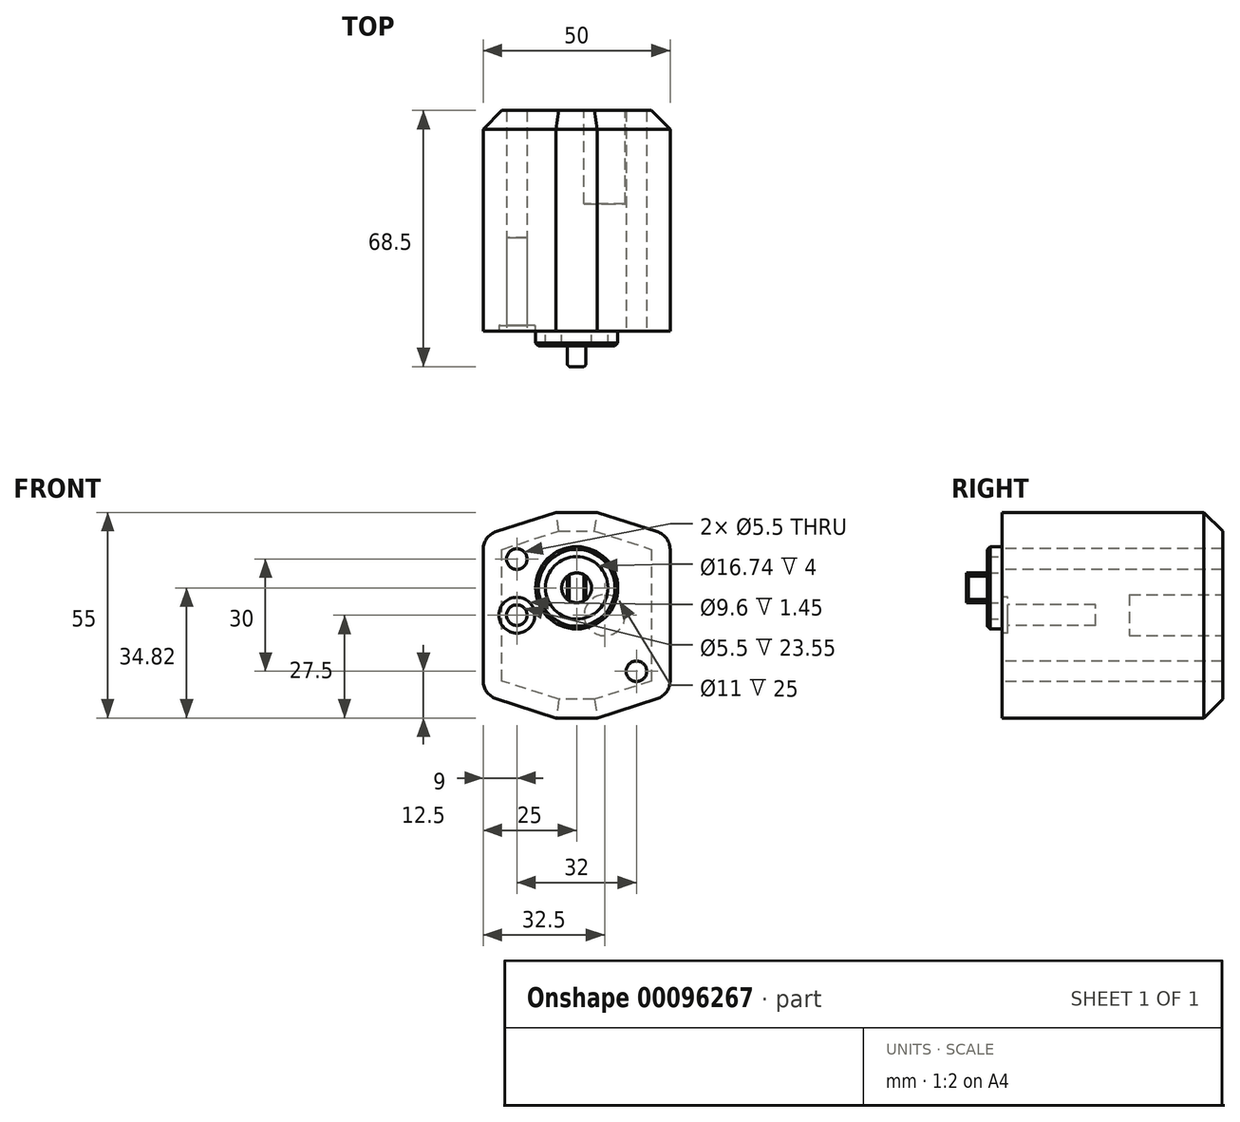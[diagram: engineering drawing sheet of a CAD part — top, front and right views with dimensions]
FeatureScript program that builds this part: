
annotation { "Feature Type Name" : "Feature", "Feature Type Description" : "" }
export const myFeature = defineFeature(function(context is Context, id is Id, definition is map)
    precondition{}
    {
        {
            var Q0;
            Q0=qCreatedBy(makeId("Front.planeOp"),FACE);
            var sketch = newSketch(context, id + "F0", { "sketchPlane" : qUnion([Q0])});
            skLineSegment(sketch, "E0", {"start": v(-25, -27.5) * mm, "end": v(25, -27.5) * mm});
            skLineSegment(sketch, "E1", {"start": v(25, -27.5) * mm, "end": v(25, 27.5) * mm});
            skLineSegment(sketch, "E2", {"start": v(25, 27.5) * mm, "end": v(-25, 27.5) * mm});
            skLineSegment(sketch, "E3", {"start": v(-25, 27.5) * mm, "end": v(-25, -27.5) * mm});
            skCircle(sketch, "E4", {"center": v(-16, 15) * mm, "radius": 2.75 * mm});
            skCircle(sketch, "E5", {"center": v(16, -15) * mm, "radius": 2.75 * mm});
            skCircle(sketch, "E6", {"center": v(-16, 0) * mm, "radius": 2.75 * mm});
            skCircle(sketch, "E7", {"center": v(0, 7.32) * mm, "radius": 4 * mm});
            skCircle(sketch, "E8", {"center": v(0, 7.32) * mm, "radius": 11 * mm});
            skLineSegment(sketch, "E9", {"start": v(-2.5, 10.44) * mm, "end": v(-2.5, 4.2) * mm});
            skLineSegment(sketch, "E10", {"start": v(2.5, 10.44) * mm, "end": v(2.5, 4.2) * mm});
            skCircle(sketch, "E11", {"center": v(0, 7.32) * mm, "radius": 8.37 * mm});
            skLineSegment(sketch, "E12", {"start": v(5.53, 27.5) * mm, "end": v(25, 21.23) * mm});
            skLineSegment(sketch, "E13.MirrorCS", {"start": v(5.53, -27.5) * mm, "end": v(25, -21.23) * mm});
            skLineSegment(sketch, "E14.MirrorCS", {"start": v(-5.53, 27.5) * mm, "end": v(-25, 21.23) * mm});
            skLineSegment(sketch, "E15.MirrorCS", {"start": v(-5.53, -27.5) * mm, "end": v(-25, -21.23) * mm});
            skCircle(sketch, "E16", {"center": v(-16, 0) * mm, "radius": 4.8 * mm});
            skSolve(sketch);
        }
        {
            var Q0;
            Q0=makeQuery(id+"F0.imprint","IMPRINT",FACE,{"disambiguationData":[TD([[makeQuery(id+"F0.imprint","IMPRINT",EDGE,{"derivedFrom":sQuery(id+"F0.wireOp",EDGE,"E4")}),-1.0]])]});
            var Q1;
            Q1=makeQuery(id+"F0.imprint","IMPRINT",FACE,{"disambiguationData":[TD([[makeQuery(id+"F0.imprint","IMPRINT",EDGE,{"derivedFrom":sQuery(id+"F0.wireOp",EDGE,"E4")}),1.0]])]});
            var Q2;
            Q2=makeQuery(id+"F0.imprint","IMPRINT",FACE,{"disambiguationData":[TD([[makeQuery(id+"F0.imprint","IMPRINT",EDGE,{"derivedFrom":sQuery(id+"F0.wireOp",EDGE,"E5")}),1.0]])]});
            var Q3;
            Q3=makeQuery(id+"F0.imprint","IMPRINT",FACE,{"disambiguationData":[TD([[makeQuery(id+"F0.imprint","IMPRINT",EDGE,{"derivedFrom":sQuery(id+"F0.wireOp",EDGE,"E6")}),-1.0]])]});
            var Q4;
            Q4=makeQuery(id+"F0.imprint","IMPRINT",FACE,{"disambiguationData":[TD([[makeQuery(id+"F0.imprint","IMPRINT",EDGE,{"derivedFrom":sQuery(id+"F0.wireOp",EDGE,"E6")}),1.0]])]});
            var Q5;
            {var subQ0=sQuery(id+"F0.wireOp",EDGE,"E9");Q5=makeQuery(id+"F0.imprint","IMPRINT",FACE,{"disambiguationData":[TD([[makeQuery(id+"F0.imprint","IMPRINT",EDGE,{"derivedFrom":subQ0}),-1.0]])]});}
            var Q6;
            {var subQ0=sQuery(id+"F0.wireOp",EDGE,"E10");Q6=makeQuery(id+"F0.imprint","IMPRINT",FACE,{"disambiguationData":[TD([[makeQuery(id+"F0.imprint","IMPRINT",EDGE,{"derivedFrom":subQ0}),1.0]])]});}
            var Q7;
            Q7=makeQuery(id+"F0.imprint","IMPRINT",FACE,{"disambiguationData":[TD([[makeQuery(id+"F0.imprint","IMPRINT",EDGE,{"derivedFrom":sQuery(id+"F0.wireOp",EDGE,"E8")}),1.0]])]});
            var Q8;
            {var subQ0=sQuery(id+"F0.wireOp",EDGE,"E9");Q8=makeQuery(id+"F0.imprint","IMPRINT",FACE,{"disambiguationData":[TD([[makeQuery(id+"F0.imprint","IMPRINT",EDGE,{"derivedFrom":subQ0}),1.0]])]});}
            var Q9;
            Q9=makeQuery(id+"F0.imprint","IMPRINT",FACE,{"disambiguationData":[TD([[makeQuery(id+"F0.imprint","IMPRINT",EDGE,{"derivedFrom":sQuery(id+"F0.wireOp",EDGE,"E11")}),1.0]])]});
            extrude(context, id + "F1", {"entities" : qUnion([Q0, Q1, Q2, Q3, Q4, Q5, Q6, Q7, Q8, Q9]), "oppositeDirection" : true, "depth" : 59 * mm});
        }
        {
            var Q0;
            Q0=makeQuery(id+"F0.imprint","IMPRINT",FACE,{"disambiguationData":[TD([[makeQuery(id+"F0.imprint","IMPRINT",EDGE,{"derivedFrom":sQuery(id+"F0.wireOp",EDGE,"E8")}),1.0]])]});
            extrude(context, id + "F2", {"entities" : qUnion([Q0]), "operationType" : NewBodyOperationType.ADD, "depth" : 4 * mm});
        }
        {
            var Q0;
            {var subQ0=sQuery(id+"F0.wireOp",EDGE,"E9");Q0=makeQuery(id+"F0.imprint","IMPRINT",FACE,{"disambiguationData":[TD([[makeQuery(id+"F0.imprint","IMPRINT",EDGE,{"derivedFrom":subQ0}),1.0]])]});}
            extrude(context, id + "F3", {"entities" : qUnion([Q0]), "operationType" : NewBodyOperationType.ADD, "depth" : 9.5 * mm});
        }
        {
            var Q0;
            {var subQ0=sQuery(id+"F0.wireOp",EDGE,"E10");Q0=makeQuery(id+"F0.imprint","IMPRINT",FACE,{"disambiguationData":[TD([[makeQuery(id+"F0.imprint","IMPRINT",EDGE,{"derivedFrom":subQ0}),1.0]])]});}
            var Q1;
            {var subQ0=sQuery(id+"F0.wireOp",EDGE,"E9");Q1=makeQuery(id+"F0.imprint","IMPRINT",FACE,{"disambiguationData":[TD([[makeQuery(id+"F0.imprint","IMPRINT",EDGE,{"derivedFrom":subQ0}),-1.0]])]});}
            extrude(context, id + "F4", {"entities" : qUnion([Q0, Q1]), "operationType" : NewBodyOperationType.ADD, "depth" : 4 * mm});
        }
        {
            var Q0;
            Q0=makeQuery(id+"F0.imprint","IMPRINT",FACE,{"disambiguationData":[TD([[makeQuery(id+"F0.imprint","IMPRINT",EDGE,{"derivedFrom":sQuery(id+"F0.wireOp",EDGE,"E4")}),1.0]])]});
            var Q1;
            Q1=makeQuery(id+"F0.imprint","IMPRINT",FACE,{"disambiguationData":[TD([[makeQuery(id+"F0.imprint","IMPRINT",EDGE,{"derivedFrom":sQuery(id+"F0.wireOp",EDGE,"E5")}),1.0]])]});
            extrude(context, id + "F5", {"entities" : qUnion([Q0, Q1]), "operationType" : NewBodyOperationType.REMOVE, "endBound" : BoundingType.THROUGH_ALL, "oppositeDirection" : true, "depth" : 20 * mm});
        }
        {
            var Q0;
            Q0=makeQuery(id+"F0.imprint","IMPRINT",FACE,{"disambiguationData":[TD([[makeQuery(id+"F0.imprint","IMPRINT",EDGE,{"derivedFrom":sQuery(id+"F0.wireOp",EDGE,"E6")}),1.0]])]});
            extrude(context, id + "F6", {"entities" : qUnion([Q0]), "operationType" : NewBodyOperationType.REMOVE, "oppositeDirection" : true, "depth" : 25 * mm});
        }
        {
            var Q0;
            Q0=makeQuery(id+"F0.imprint","IMPRINT",FACE,{"disambiguationData":[TD([[makeQuery(id+"F0.imprint","IMPRINT",EDGE,{"derivedFrom":sQuery(id+"F0.wireOp",EDGE,"E6")}),-1.0]])]});
            extrude(context, id + "F7", {"entities" : qUnion([Q0]), "operationType" : NewBodyOperationType.REMOVE, "oppositeDirection" : true, "depth" : 1.45 * mm});
        }
        {
            var Q0;
            Q0=makeQuery(id+"F1.opExtrude","SWEPT_EDGE",EDGE,{"disambiguationData":[OSD([sQuery(id+"F0.wireOp",EDGE,"E1"),sQuery(id+"F0.wireOp",EDGE,"E12")])]});
            var Q1;
            Q1=makeQuery(id+"F1.opExtrude","SWEPT_EDGE",EDGE,{"disambiguationData":[OSD([sQuery(id+"F0.wireOp",EDGE,"E1"),sQuery(id+"F0.wireOp",EDGE,"E13.MirrorCS")])]});
            var Q2;
            Q2=makeQuery(id+"F1.opExtrude","SWEPT_EDGE",EDGE,{"disambiguationData":[OSD([sQuery(id+"F0.wireOp",EDGE,"E3"),sQuery(id+"F0.wireOp",EDGE,"E14.MirrorCS")])]});
            var Q3;
            Q3=makeQuery(id+"F1.opExtrude","SWEPT_EDGE",EDGE,{"disambiguationData":[OSD([sQuery(id+"F0.wireOp",EDGE,"E3"),sQuery(id+"F0.wireOp",EDGE,"E15.MirrorCS")])]});
            fillet(context, id + "F8", {"entities" : qUnion([Q0, Q1, Q2, Q3]), "radius" : 5 * mm, "tangentPropagation" : true, "allowEdgeOverflow" : false});
        }
        {
            var Q0;
            Q0=makeQuery(id+"F1.opExtrude","CAP_EDGE",EDGE,{"disambiguationData":[OSD([sQuery(id+"F0.wireOp",EDGE,"E1")])],"isStart":false});
            var Q1;
            Q1=makeQuery(id+"F1.opExtrude","CAP_EDGE",EDGE,{"disambiguationData":[OSD([sQuery(id+"F0.wireOp",EDGE,"E3")])],"isStart":false});
            var Q2;
            Q2=makeQuery(id+"F1.opExtrude","CAP_EDGE",EDGE,{"disambiguationData":[OSD([sQuery(id+"F0.wireOp",EDGE,"E2")])],"isStart":false});
            var Q3;
            Q3=makeQuery(id+"F1.opExtrude","CAP_EDGE",EDGE,{"disambiguationData":[OSD([sQuery(id+"F0.wireOp",EDGE,"E0")])],"isStart":false});
            chamfer(context, id + "F9", {"entities" : qUnion([Q0, Q1, Q2, Q3]), "width" : 5 * mm, "tangentPropagation" : true});
        }
        {
            var Q0;
            Q0=makeQuery(id+"F3.opExtrude","CAP_EDGE",EDGE,{"disambiguationData":[OSD([sQuery(id+"F0.wireOp",EDGE,"E10")])],"isStart":false});
            var Q1;
            Q1=makeQuery(id+"F3.opExtrude","CAP_EDGE",EDGE,{"disambiguationData":[OSD([sQuery(id+"F0.wireOp",EDGE,"E9")])],"isStart":false});
            chamfer(context, id + "F10", {"entities" : qUnion([Q0, Q1]), "width" : 0.5 * mm, "tangentPropagation" : true});
        }
        {
            var Q0;
            Q0=makeQuery(id+"F1.opExtrude","CAP_FACE",FACE,{"disambiguationData":[OSD([sQuery(id+"F0.wireOp",EDGE,"E0"),sQuery(id+"F0.wireOp",EDGE,"E1"),sQuery(id+"F0.wireOp",EDGE,"E2"),sQuery(id+"F0.wireOp",EDGE,"E3"),sQuery(id+"F0.wireOp",EDGE,"E12"),sQuery(id+"F0.wireOp",EDGE,"E13.MirrorCS"),sQuery(id+"F0.wireOp",EDGE,"E14.MirrorCS"),sQuery(id+"F0.wireOp",EDGE,"E15.MirrorCS")])],"isStart":false});
            var sketch = newSketch(context, id + "F11", { "sketchPlane" : qUnion([Q0])});
            skCircle(sketch, "E17", {"center": v(-7.5, 0) * mm, "radius": 5.5 * mm});
            skSolve(sketch);
        }
        {
            var Q0;
            Q0=makeQuery(id+"F11.imprint","IMPRINT",FACE,{"disambiguationData":[TD([[makeQuery(id+"F11.imprint","IMPRINT",EDGE,{"derivedFrom":sQuery(id+"F11.wireOp",EDGE,"E17")}),1.0]])]});
            extrude(context, id + "F12", {"entities" : qUnion([Q0]), "operationType" : NewBodyOperationType.REMOVE, "oppositeDirection" : true, "depth" : 25 * mm});
        }
        {
            var Q0;
            Q0=makeQuery(id+"F2.opExtrude","CAP_EDGE",EDGE,{"disambiguationData":[OSD([sQuery(id+"F0.wireOp",EDGE,"E8")])],"isStart":false});
            chamfer(context, id + "F13", {"entities" : qUnion([Q0]), "width" : 0.75 * mm, "tangentPropagation" : true});
        }
    });
